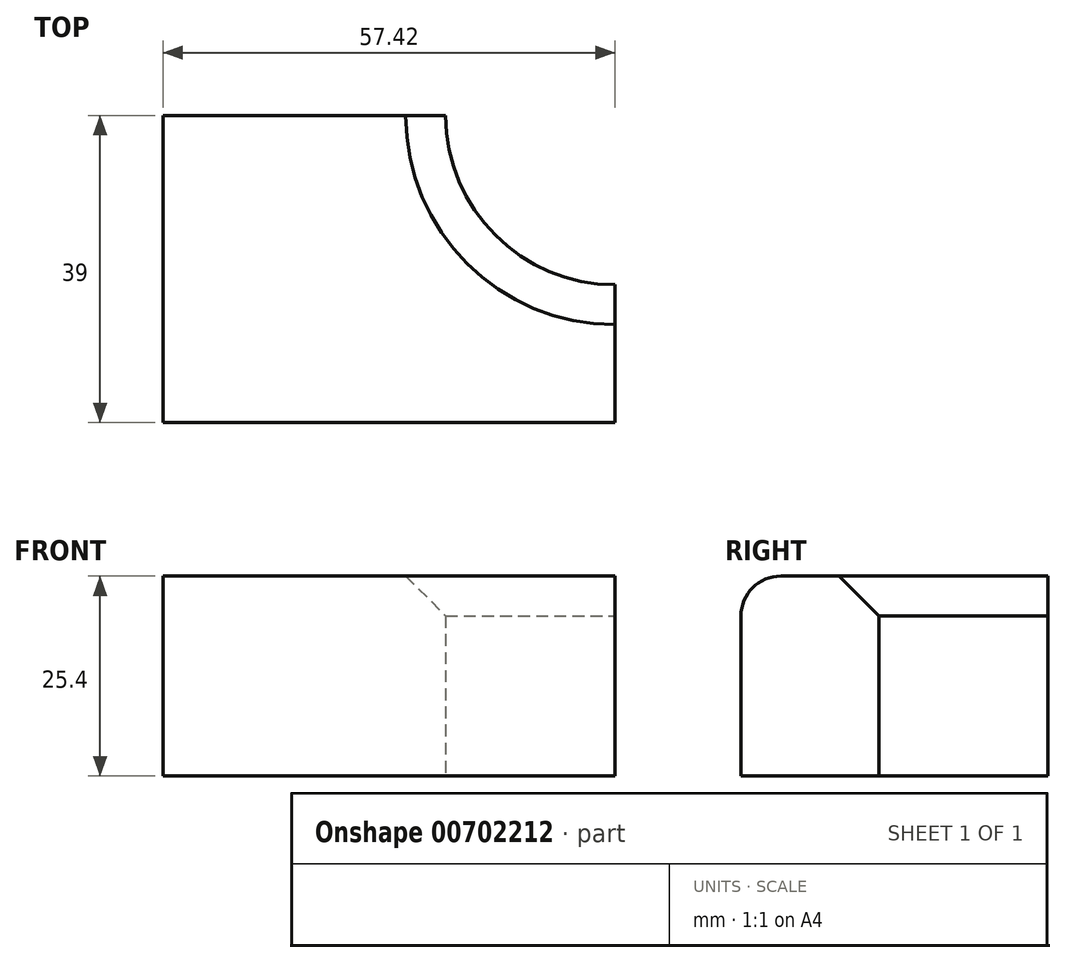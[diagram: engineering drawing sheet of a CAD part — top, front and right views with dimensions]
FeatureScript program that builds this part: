
annotation { "Feature Type Name" : "Feature", "Feature Type Description" : "" }
export const myFeature = defineFeature(function(context is Context, id is Id, definition is map)
    precondition{}
    {
        {
            var Q0;
            Q0=qCreatedBy(makeId("Top.planeOp"),FACE);
            var sketch = newSketch(context, id + "F0", { "sketchPlane" : qUnion([Q0])});
            skCircle(sketch, "E0", {"center": v(0, 0) * mm, "radius": 21.5 * mm});
            skLineSegment(sketch, "E1.bottom", {"start": v(0, 0) * mm, "end": v(-57.42, 0) * mm});
            skLineSegment(sketch, "E1.top", {"start": v(0, -39) * mm, "end": v(-57.42, -39) * mm});
            skLineSegment(sketch, "E1.left", {"start": v(0, 0) * mm, "end": v(0, -39) * mm});
            skLineSegment(sketch, "E1.right", {"start": v(-57.42, 0) * mm, "end": v(-57.42, -39) * mm});
            skSolve(sketch);
        }
        {
            var Q0;
            {var subQ1=sQuery(id+"F0.wireOp",EDGE,"E1.top");Q0=makeQuery(id+"F0.imprint","IMPRINT",FACE,{"disambiguationData":[TD([[makeQuery(id+"F0.imprint","IMPRINT",EDGE,{"derivedFrom":subQ1}),-1.0]])]});}
            extrude(context, id + "F1", {"entities" : qUnion([Q0]), "depth" : 25.4 * mm, "offsetDistance" : 25.4 * mm});
        }
        {
            var Q0;
            Q0=makeQuery(id+"F1.opExtrude","CAP_EDGE",EDGE,{"disambiguationData":[OSD([sQuery(id+"F0.wireOp",EDGE,"E1.top")])],"isStart":false});
            fillet(context, id + "F2", {"entities" : qUnion([Q0]), "radius" : 5.08 * mm, "tangentPropagation" : true, "allowEdgeOverflow" : false});
        }
        {
            var Q0;
            Q0=makeQuery(id+"F1.opExtrude","CAP_EDGE",EDGE,{"disambiguationData":[OSD([sQuery(id+"F0.wireOp",EDGE,"E0")])],"isStart":false});
            chamfer(context, id + "F3", {"entities" : qUnion([Q0]), "width" : 5.08 * mm, "tangentPropagation" : true});
        }
    });
